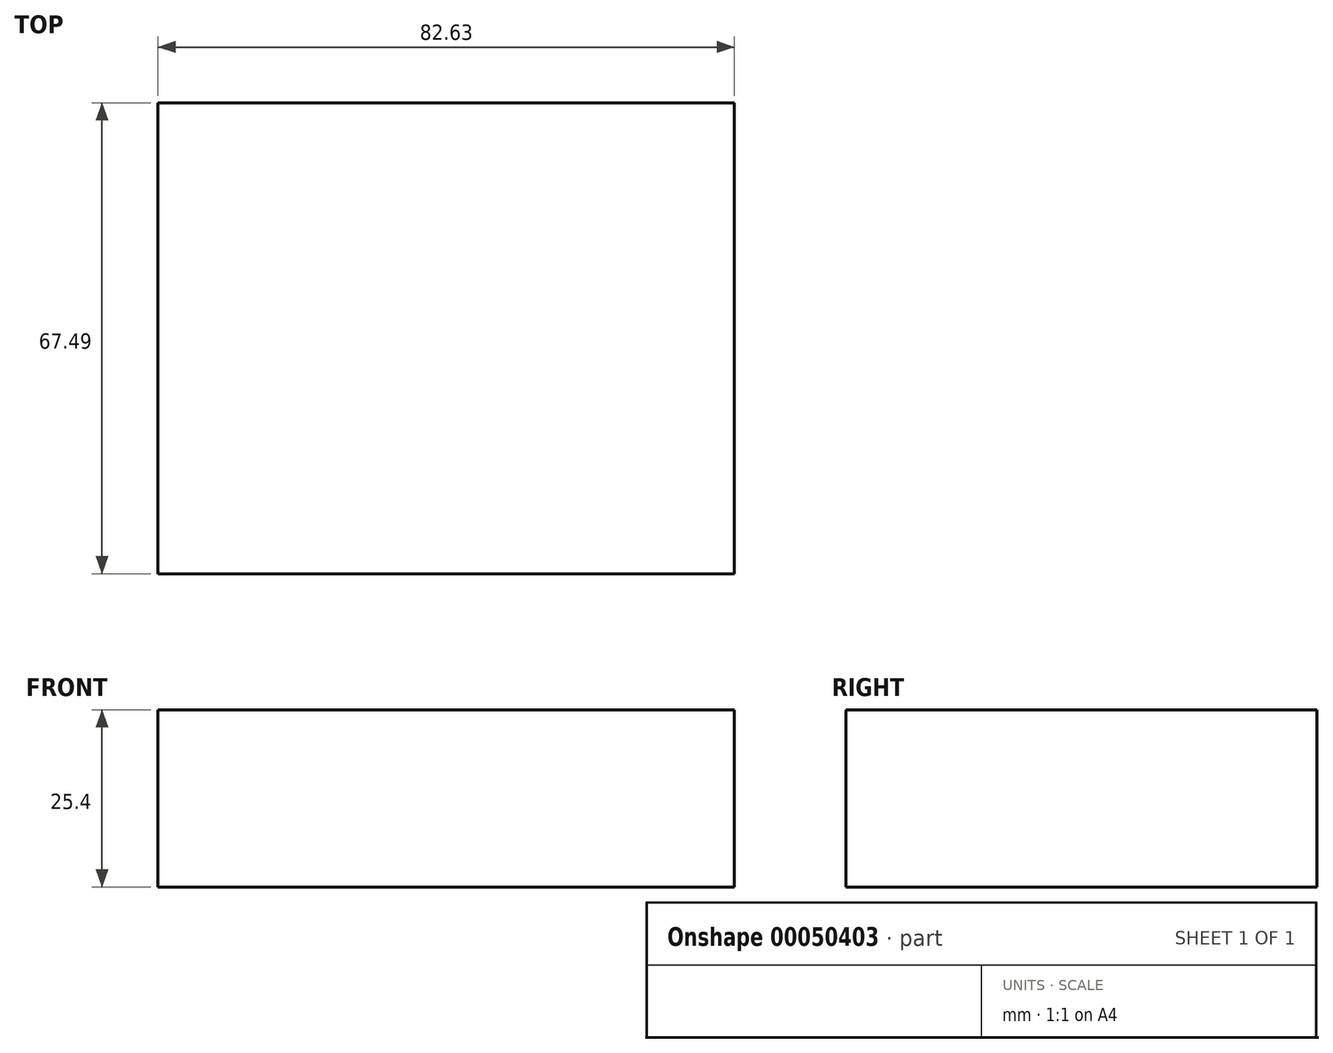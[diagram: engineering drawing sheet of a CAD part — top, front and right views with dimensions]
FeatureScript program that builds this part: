
annotation { "Feature Type Name" : "Feature", "Feature Type Description" : "" }
export const myFeature = defineFeature(function(context is Context, id is Id, definition is map)
    precondition{}
    {
        {
            var Q0;
            Q0=qCreatedBy(makeId("Top.planeOp"),FACE);
            var sketch = newSketch(context, id + "F0", { "sketchPlane" : qUnion([Q0])});
            skLineSegment(sketch, "E0.bottom", {"start": v(-30.9, 31.54) * mm, "end": v(51.72, 31.54) * mm});
            skLineSegment(sketch, "E0.top", {"start": v(-30.9, -35.95) * mm, "end": v(51.72, -35.95) * mm});
            skLineSegment(sketch, "E0.left", {"start": v(-30.9, 31.54) * mm, "end": v(-30.9, -35.95) * mm});
            skLineSegment(sketch, "E0.right", {"start": v(51.72, 31.54) * mm, "end": v(51.72, -35.95) * mm});
            skSolve(sketch);
        }
        {
            var Q0;
            Q0=makeQuery(id+"F0.imprint","IMPRINT",FACE,{"disambiguationData":[TD([[makeQuery(id+"F0.imprint","IMPRINT",EDGE,{"derivedFrom":sQuery(id+"F0.wireOp",EDGE,"E0.bottom")}),-1.0]])]});
            extrude(context, id + "F1", {"entities" : qUnion([Q0]), "depth" : 25.4 * mm});
        }
    });
